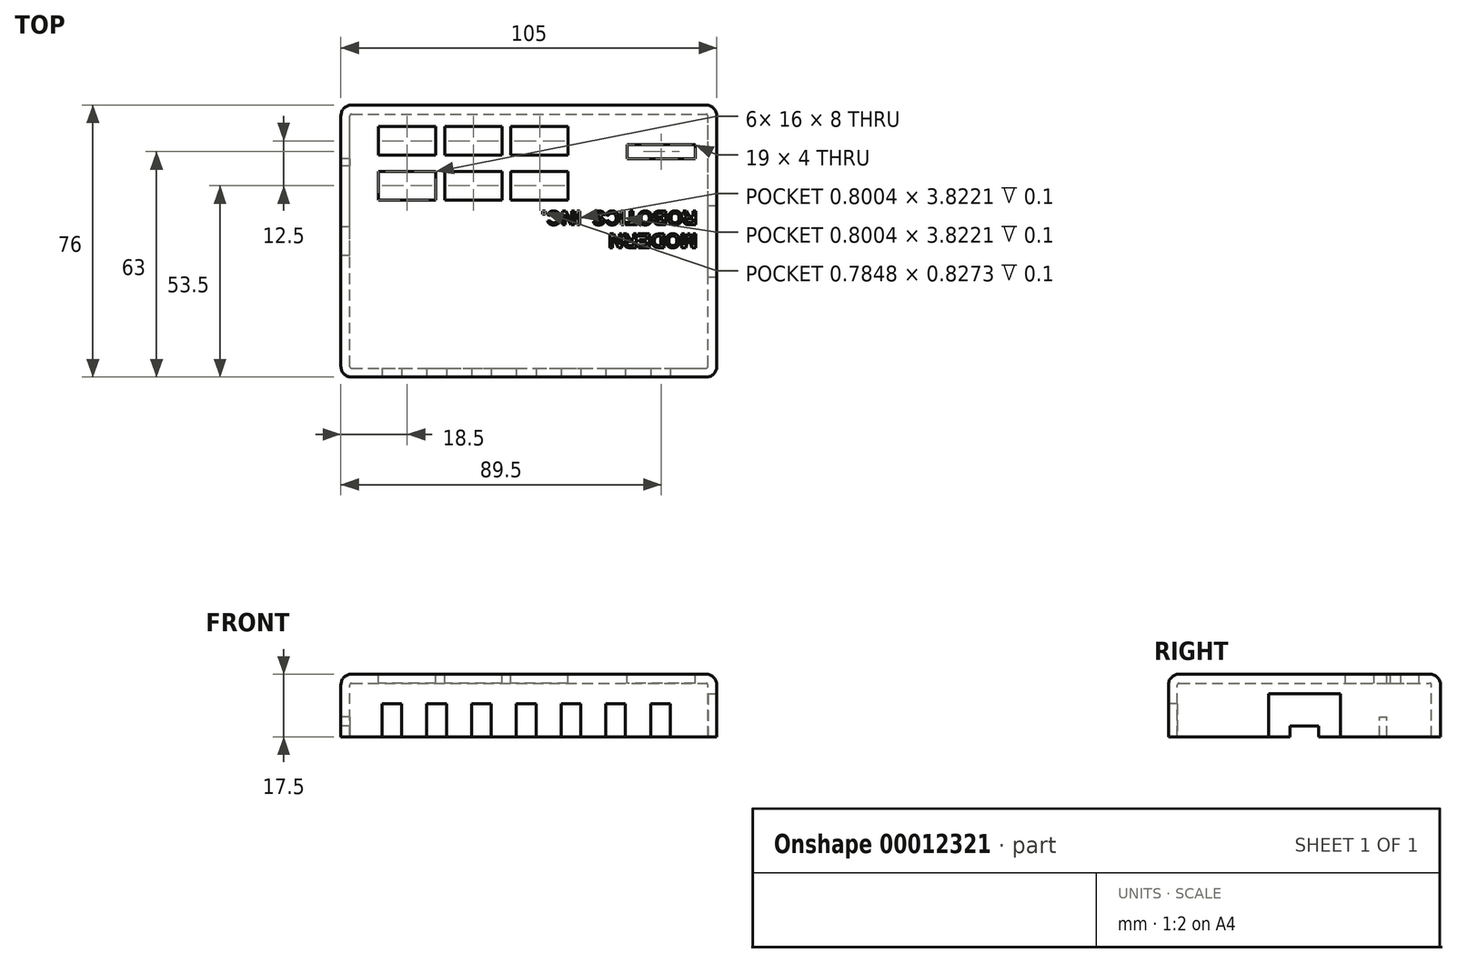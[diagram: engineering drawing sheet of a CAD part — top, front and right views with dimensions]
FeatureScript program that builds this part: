
annotation { "Feature Type Name" : "Feature", "Feature Type Description" : "" }
export const myFeature = defineFeature(function(context is Context, id is Id, definition is map)
    precondition{}
    {
        {
            var Q0;
            Q0=qCreatedBy(makeId("Top.planeOp"),FACE);
            var sketch = newSketch(context, id + "F0", { "sketchPlane" : qUnion([Q0])});
            skLineSegment(sketch, "E0.bottom", {"start": v(0, 0) * mm, "end": v(105, 0) * mm});
            skLineSegment(sketch, "E0.top", {"start": v(0, 76) * mm, "end": v(105, 76) * mm});
            skLineSegment(sketch, "E0.left", {"start": v(0, 0) * mm, "end": v(0, 76) * mm});
            skLineSegment(sketch, "E0.right", {"start": v(105, 0) * mm, "end": v(105, 76) * mm});
            skSolve(sketch);
        }
        {
            var Q0;
            Q0=qSketchRegion(id+"F0",true);
            extrude(context, id + "F1", {"entities" : qUnion([Q0]), "depth" : 17.5 * mm});
        }
        {
            var Q0;
            Q0=makeQuery(id+"F1.opExtrude","SWEPT_EDGE",EDGE,{"disambiguationData":[OSD([sQuery(id+"F0.wireOp",EDGE,"E0.bottom"),sQuery(id+"F0.wireOp",EDGE,"E0.left")])]});
            var Q1;
            Q1=makeQuery(id+"F1.opExtrude","CAP_EDGE",EDGE,{"disambiguationData":[OSD([sQuery(id+"F0.wireOp",EDGE,"E0.bottom")])],"isStart":false});
            var Q2;
            Q2=makeQuery(id+"F1.opExtrude","CAP_EDGE",EDGE,{"disambiguationData":[OSD([sQuery(id+"F0.wireOp",EDGE,"E0.left")])],"isStart":false});
            var Q3;
            Q3=makeQuery(id+"F1.opExtrude","SWEPT_EDGE",EDGE,{"disambiguationData":[OSD([sQuery(id+"F0.wireOp",EDGE,"E0.bottom"),sQuery(id+"F0.wireOp",EDGE,"E0.right")])]});
            var Q4;
            Q4=makeQuery(id+"F1.opExtrude","CAP_EDGE",EDGE,{"disambiguationData":[OSD([sQuery(id+"F0.wireOp",EDGE,"E0.right")])],"isStart":false});
            var Q5;
            Q5=makeQuery(id+"F1.opExtrude","CAP_EDGE",EDGE,{"disambiguationData":[OSD([sQuery(id+"F0.wireOp",EDGE,"E0.top")])],"isStart":false});
            var Q6;
            Q6=makeQuery(id+"F1.opExtrude","SWEPT_EDGE",EDGE,{"disambiguationData":[OSD([sQuery(id+"F0.wireOp",EDGE,"E0.top"),sQuery(id+"F0.wireOp",EDGE,"E0.right")])]});
            var Q7;
            Q7=makeQuery(id+"F1.opExtrude","SWEPT_EDGE",EDGE,{"disambiguationData":[OSD([sQuery(id+"F0.wireOp",EDGE,"E0.top"),sQuery(id+"F0.wireOp",EDGE,"E0.left")])]});
            fillet(context, id + "F2", {"entities" : qUnion([Q0, Q1, Q2, Q3, Q4, Q5, Q6, Q7]), "radius" : 3 * mm, "tangentPropagation" : true, "allowEdgeOverflow" : false});
        }
        {
            var Q0;
            Q0=makeQuery(id+"F1.opExtrude","CAP_FACE",FACE,{"disambiguationData":[OSD([sQuery(id+"F0.wireOp",EDGE,"E0.bottom"),sQuery(id+"F0.wireOp",EDGE,"E0.top"),sQuery(id+"F0.wireOp",EDGE,"E0.left"),sQuery(id+"F0.wireOp",EDGE,"E0.right")])],"isStart":true});
            shell(context, id + "F3", {"entities" : qUnion([Q0]), "thickness" : 2.5 * mm});
        }
        {
            var Q0;
            Q0=makeQuery(id+"F1.opExtrude","CAP_FACE",FACE,{"disambiguationData":[OSD([sQuery(id+"F0.wireOp",EDGE,"E0.bottom"),sQuery(id+"F0.wireOp",EDGE,"E0.top"),sQuery(id+"F0.wireOp",EDGE,"E0.left"),sQuery(id+"F0.wireOp",EDGE,"E0.right")])],"isStart":false});
            var sketch = newSketch(context, id + "F4", { "sketchPlane" : qUnion([Q0])});
            skLineSegment(sketch, "E1.bottom", {"start": v(10.5, 70) * mm, "end": v(26.5, 70) * mm});
            skLineSegment(sketch, "E1.top", {"start": v(10.5, 62) * mm, "end": v(26.5, 62) * mm});
            skLineSegment(sketch, "E1.left", {"start": v(10.5, 70) * mm, "end": v(10.5, 62) * mm});
            skLineSegment(sketch, "E1.right", {"start": v(26.5, 70) * mm, "end": v(26.5, 62) * mm});
            skLineSegment(sketch, "E2.0.1.0", {"start": v(10.5, 49.5) * mm, "end": v(26.5, 49.5) * mm});
            skLineSegment(sketch, "E2.0.1.1", {"start": v(26.5, 57.5) * mm, "end": v(26.5, 49.5) * mm});
            skLineSegment(sketch, "E2.0.1.2", {"start": v(10.5, 57.5) * mm, "end": v(10.5, 49.5) * mm});
            skLineSegment(sketch, "E2.0.1.3", {"start": v(10.5, 57.5) * mm, "end": v(26.5, 57.5) * mm});
            skLineSegment(sketch, "E2.1.0.0", {"start": v(29, 62) * mm, "end": v(45, 62) * mm});
            skLineSegment(sketch, "E2.1.0.1", {"start": v(45, 70) * mm, "end": v(45, 62) * mm});
            skLineSegment(sketch, "E2.1.0.2", {"start": v(29, 70) * mm, "end": v(29, 62) * mm});
            skLineSegment(sketch, "E2.1.0.3", {"start": v(29, 70) * mm, "end": v(45, 70) * mm});
            skLineSegment(sketch, "E2.1.1.0", {"start": v(29, 49.5) * mm, "end": v(45, 49.5) * mm});
            skLineSegment(sketch, "E2.1.1.1", {"start": v(45, 57.5) * mm, "end": v(45, 49.5) * mm});
            skLineSegment(sketch, "E2.1.1.2", {"start": v(29, 57.5) * mm, "end": v(29, 49.5) * mm});
            skLineSegment(sketch, "E2.1.1.3", {"start": v(29, 57.5) * mm, "end": v(45, 57.5) * mm});
            skLineSegment(sketch, "E2.2.0.0", {"start": v(47.5, 62) * mm, "end": v(63.5, 62) * mm});
            skLineSegment(sketch, "E2.2.0.1", {"start": v(63.5, 70) * mm, "end": v(63.5, 62) * mm});
            skLineSegment(sketch, "E2.2.0.2", {"start": v(47.5, 70) * mm, "end": v(47.5, 62) * mm});
            skLineSegment(sketch, "E2.2.0.3", {"start": v(47.5, 70) * mm, "end": v(63.5, 70) * mm});
            skLineSegment(sketch, "E2.2.1.0", {"start": v(47.5, 49.5) * mm, "end": v(63.5, 49.5) * mm});
            skLineSegment(sketch, "E2.2.1.1", {"start": v(63.5, 57.5) * mm, "end": v(63.5, 49.5) * mm});
            skLineSegment(sketch, "E2.2.1.2", {"start": v(47.5, 57.5) * mm, "end": v(47.5, 49.5) * mm});
            skLineSegment(sketch, "E2.2.1.3", {"start": v(47.5, 57.5) * mm, "end": v(63.5, 57.5) * mm});
            skLineSegment(sketch, "E2.direction1", {"start": v(10.5, 62) * mm, "end": v(29, 62) * mm, "construction": true});
            skLineSegment(sketch, "E2.direction2", {"start": v(10.5, 62) * mm, "end": v(10.5, 49.5) * mm, "construction": true});
            skLineSegment(sketch, "E3.bottom", {"start": v(80, 65) * mm, "end": v(99, 65) * mm});
            skLineSegment(sketch, "E3.top", {"start": v(80, 61) * mm, "end": v(99, 61) * mm});
            skLineSegment(sketch, "E3.left", {"start": v(80, 65) * mm, "end": v(80, 61) * mm});
            skLineSegment(sketch, "E3.right", {"start": v(99, 65) * mm, "end": v(99, 61) * mm});
            skSolve(sketch);
        }
        {
            var Q0;
            Q0=qSketchRegion(id+"F4",true);
            extrude(context, id + "F5", {"entities" : qUnion([Q0]), "operationType" : NewBodyOperationType.REMOVE, "endBound" : BoundingType.UP_TO_NEXT, "oppositeDirection" : true, "depth" : 25 * mm});
        }
        {
            var Q0;
            Q0=makeQuery(id+"F1.opExtrude","SWEPT_FACE",FACE,{"disambiguationData":[OSD([sQuery(id+"F0.wireOp",EDGE,"E0.bottom")])]});
            var sketch = newSketch(context, id + "F6", { "sketchPlane" : qUnion([Q0])});
            skLineSegment(sketch, "E4.bottom", {"start": v(11.5, 9.23) * mm, "end": v(17, 9.23) * mm});
            skLineSegment(sketch, "E4.top", {"start": v(11.5, 0) * mm, "end": v(17, 0) * mm});
            skLineSegment(sketch, "E4.left", {"start": v(11.5, 9.23) * mm, "end": v(11.5, 0) * mm});
            skLineSegment(sketch, "E4.right", {"start": v(17, 9.23) * mm, "end": v(17, 0) * mm});
            skLineSegment(sketch, "E5.1.0.0", {"start": v(24, 9.23) * mm, "end": v(29.5, 9.23) * mm});
            skLineSegment(sketch, "E5.1.0.1", {"start": v(24, 9.23) * mm, "end": v(24, 0) * mm});
            skLineSegment(sketch, "E5.1.0.2", {"start": v(24, 0) * mm, "end": v(29.5, 0) * mm});
            skLineSegment(sketch, "E5.1.0.3", {"start": v(29.5, 9.23) * mm, "end": v(29.5, 0) * mm});
            skLineSegment(sketch, "E5.2.0.0", {"start": v(36.5, 9.23) * mm, "end": v(42, 9.23) * mm});
            skLineSegment(sketch, "E5.2.0.1", {"start": v(36.5, 9.23) * mm, "end": v(36.5, 0) * mm});
            skLineSegment(sketch, "E5.2.0.2", {"start": v(36.5, 0) * mm, "end": v(42, 0) * mm});
            skLineSegment(sketch, "E5.2.0.3", {"start": v(42, 9.23) * mm, "end": v(42, 0) * mm});
            skLineSegment(sketch, "E5.3.0.0", {"start": v(49, 9.23) * mm, "end": v(54.5, 9.23) * mm});
            skLineSegment(sketch, "E5.3.0.1", {"start": v(49, 9.23) * mm, "end": v(49, 0) * mm});
            skLineSegment(sketch, "E5.3.0.2", {"start": v(49, 0) * mm, "end": v(54.5, 0) * mm});
            skLineSegment(sketch, "E5.3.0.3", {"start": v(54.5, 9.23) * mm, "end": v(54.5, 0) * mm});
            skLineSegment(sketch, "E5.4.0.0", {"start": v(61.5, 9.23) * mm, "end": v(67, 9.23) * mm});
            skLineSegment(sketch, "E5.4.0.1", {"start": v(61.5, 9.23) * mm, "end": v(61.5, 0) * mm});
            skLineSegment(sketch, "E5.4.0.2", {"start": v(61.5, 0) * mm, "end": v(67, 0) * mm});
            skLineSegment(sketch, "E5.4.0.3", {"start": v(67, 9.23) * mm, "end": v(67, 0) * mm});
            skLineSegment(sketch, "E5.5.0.0", {"start": v(74, 9.23) * mm, "end": v(79.5, 9.23) * mm});
            skLineSegment(sketch, "E5.5.0.1", {"start": v(74, 9.23) * mm, "end": v(74, 0) * mm});
            skLineSegment(sketch, "E5.5.0.2", {"start": v(74, 0) * mm, "end": v(79.5, 0) * mm});
            skLineSegment(sketch, "E5.5.0.3", {"start": v(79.5, 9.23) * mm, "end": v(79.5, 0) * mm});
            skLineSegment(sketch, "E5.6.0.0", {"start": v(86.5, 9.23) * mm, "end": v(92, 9.23) * mm});
            skLineSegment(sketch, "E5.6.0.1", {"start": v(86.5, 9.23) * mm, "end": v(86.5, 0) * mm});
            skLineSegment(sketch, "E5.6.0.2", {"start": v(86.5, 0) * mm, "end": v(92, 0) * mm});
            skLineSegment(sketch, "E5.6.0.3", {"start": v(92, 9.23) * mm, "end": v(92, 0) * mm});
            skLineSegment(sketch, "E5.direction1", {"start": v(11, 9.23) * mm, "end": v(23.5, 9.23) * mm, "construction": true});
            skSolve(sketch);
        }
        {
            var Q0;
            Q0=qSketchRegion(id+"F6",true);
            extrude(context, id + "F7", {"entities" : qUnion([Q0]), "operationType" : NewBodyOperationType.REMOVE, "endBound" : BoundingType.UP_TO_NEXT, "oppositeDirection" : true, "depth" : 25 * mm});
        }
        {
            var Q0;
            Q0=makeQuery(id+"F1.opExtrude","SWEPT_FACE",FACE,{"disambiguationData":[OSD([sQuery(id+"F0.wireOp",EDGE,"E0.right")])]});
            var sketch = newSketch(context, id + "F8", { "sketchPlane" : qUnion([Q0])});
            skLineSegment(sketch, "E6.bottom", {"start": v(28, 12) * mm, "end": v(48, 12) * mm});
            skLineSegment(sketch, "E6.top", {"start": v(28, 0) * mm, "end": v(48, 0) * mm});
            skLineSegment(sketch, "E6.left", {"start": v(28, 12) * mm, "end": v(28, 0) * mm});
            skLineSegment(sketch, "E6.right", {"start": v(48, 12) * mm, "end": v(48, 0) * mm});
            skPoint(sketch, "E7", {"position": v(38, 0) * mm});
            skPoint(sketch, "E8", {"position": v(100.9, 31.9) * mm});
            skSolve(sketch);
        }
        {
            var Q0;
            Q0=qSketchRegion(id+"F8",true);
            extrude(context, id + "F9", {"entities" : qUnion([Q0]), "operationType" : NewBodyOperationType.REMOVE, "endBound" : BoundingType.UP_TO_NEXT, "oppositeDirection" : true, "depth" : 25 * mm});
        }
        {
            var Q0;
            Q0=makeQuery(id+"F1.opExtrude","SWEPT_FACE",FACE,{"disambiguationData":[OSD([sQuery(id+"F0.wireOp",EDGE,"E0.left")])]});
            var sketch = newSketch(context, id + "F10", { "sketchPlane" : qUnion([Q0])});
            skLineSegment(sketch, "E9.bottom", {"start": v(-59, 0) * mm, "end": v(-61, 0) * mm});
            skLineSegment(sketch, "E9.top", {"start": v(-59, 5.5) * mm, "end": v(-61, 5.5) * mm});
            skLineSegment(sketch, "E9.left", {"start": v(-59, 0) * mm, "end": v(-59, 5.5) * mm});
            skLineSegment(sketch, "E9.right", {"start": v(-61, 0) * mm, "end": v(-61, 5.5) * mm});
            skLineSegment(sketch, "E10.bottom", {"start": v(-42, 0) * mm, "end": v(-34, 0) * mm});
            skLineSegment(sketch, "E10.top", {"start": v(-42, 3) * mm, "end": v(-34, 3) * mm});
            skLineSegment(sketch, "E10.left", {"start": v(-42, 0) * mm, "end": v(-42, 3) * mm});
            skLineSegment(sketch, "E10.right", {"start": v(-34, 0) * mm, "end": v(-34, 3) * mm});
            skPoint(sketch, "E11", {"position": v(-38, 0) * mm});
            skSolve(sketch);
        }
        {
            var Q0;
            Q0=qSketchRegion(id+"F10",true);
            extrude(context, id + "F11", {"entities" : qUnion([Q0]), "operationType" : NewBodyOperationType.REMOVE, "endBound" : BoundingType.UP_TO_NEXT, "oppositeDirection" : true, "depth" : 25 * mm});
        }
        {
            var Q0;
            Q0=makeQuery(id+"F4.imprint","IMPRINT",FACE,{"disambiguationData":[TD([[makeQuery(id+"F4.imprint","IMPRINT",EDGE,{"derivedFrom":sQuery(id+"F4.wireOp",EDGE,"E1.bottom")}),1.0]])]});
            var sketch = newSketch(context, id + "F12", { "sketchPlane" : qUnion([Q0])});
            skText(sketch, "E12", { "text": "MODERN\nROBOTICS  INC.", "fontName": "Arimo-Bold.ttf"});
            const initialGuessF12  = {"E12": [0.0995, 0.04, -1, 0, 0.004]};
            skSetInitialGuess(sketch, initialGuessF12);
            skSolve(sketch);
        }
        {
            var Q0;
            Q0=qSketchRegion(id+"F12",true);
            extrude(context, id + "F13", {"entities" : qUnion([Q0]), "operationType" : NewBodyOperationType.REMOVE, "oppositeDirection" : true, "depth" : .1 * mm});
        }
    });
